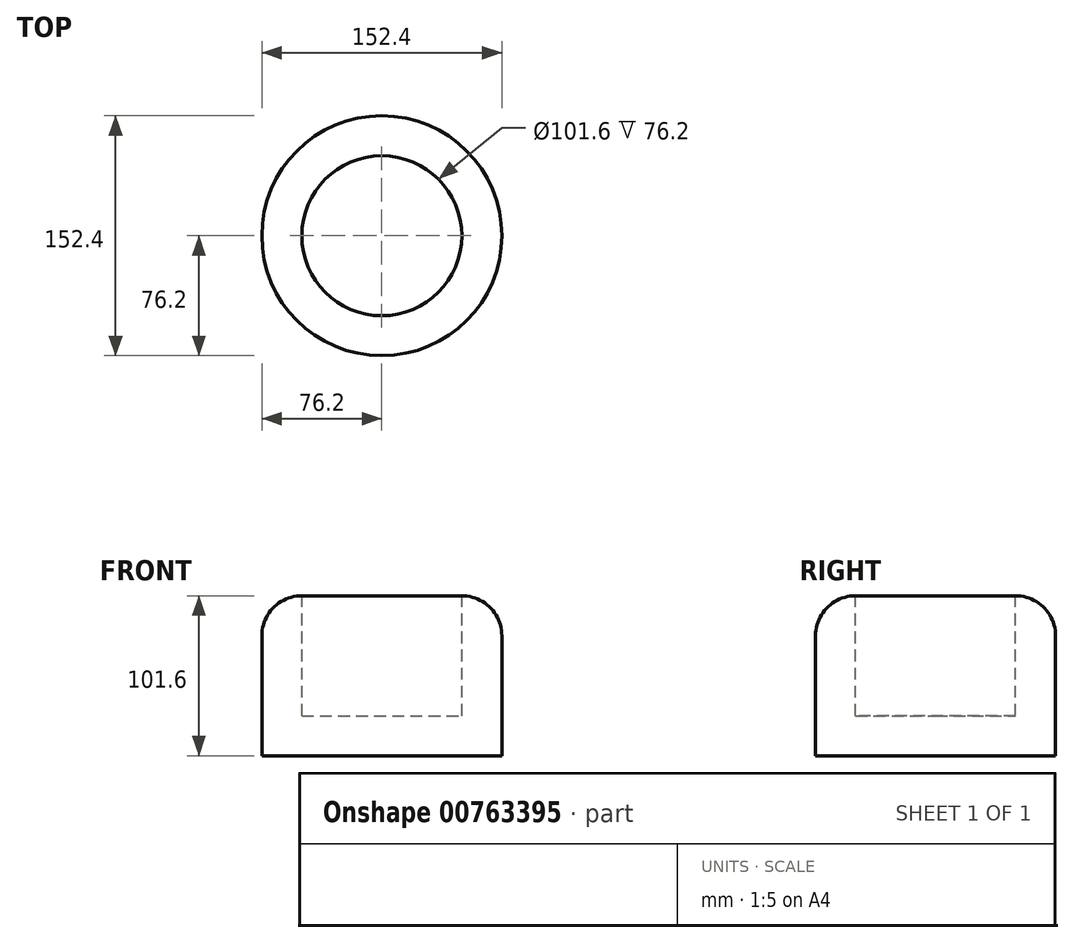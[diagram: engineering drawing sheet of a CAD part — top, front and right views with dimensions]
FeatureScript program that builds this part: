
annotation { "Feature Type Name" : "Feature", "Feature Type Description" : "" }
export const myFeature = defineFeature(function(context is Context, id is Id, definition is map)
    precondition{}
    {
        {
            var Q0;
            Q0=qCreatedBy(makeId("Front.planeOp"),FACE);
            var sketch = newSketch(context, id + "F0", { "sketchPlane" : qUnion([Q0])});
            skLineSegment(sketch, "E0.bottom", {"start": v(-76.2, 50.8) * mm, "end": v(0, 50.8) * mm});
            skLineSegment(sketch, "E0.top", {"start": v(-76.2, -50.8) * mm, "end": v(0, -50.8) * mm});
            skLineSegment(sketch, "E0.left", {"start": v(-76.2, 50.8) * mm, "end": v(-76.2, -50.8) * mm});
            skLineSegment(sketch, "E0.right", {"start": v(0, 50.8) * mm, "end": v(0, -50.8) * mm});
            skSolve(sketch);
        }
        {
            var Q0;
            Q0=makeQuery(id+"F0.imprint","IMPRINT",FACE,{"disambiguationData":[TD([[makeQuery(id+"F0.imprint","IMPRINT",EDGE,{"derivedFrom":sQuery(id+"F0.wireOp",EDGE,"E0.bottom")}),-1.0]])]});
            var Q1;
            Q1=sQuery(id+"F0.wireOp",EDGE,"E0.right");
            revolve(context, id + "F1", {"surfaceOperationType" : NewSurfaceOperationType.NEW, "entities" : qUnion([Q0]), "axis" : qUnion([Q1]), "revolveType" : RevolveType.FULL});
        }
        {
            var Q0;
            Q0=makeQuery(id+"F1.opRevolve","SWEPT_EDGE",EDGE,{"disambiguationData":[OSD([sQuery(id+"F0.wireOp",EDGE,"E0.bottom"),sQuery(id+"F0.wireOp",EDGE,"E0.left")])]});
            fillet(context, id + "F2", {"entities" : qUnion([Q0]), "radius" : 25.4 * mm, "tangentPropagation" : true, "allowEdgeOverflow" : false});
        }
        {
            var Q0;
            Q0=makeQuery(id+"F1.opRevolve","SWEPT_FACE",FACE,{"disambiguationData":[OSD([sQuery(id+"F0.wireOp",EDGE,"E0.bottom")])]});
            shell(context, id + "F3", {"entities" : qUnion([Q0]), "thickness" : 25.4 * mm});
        }
    });
